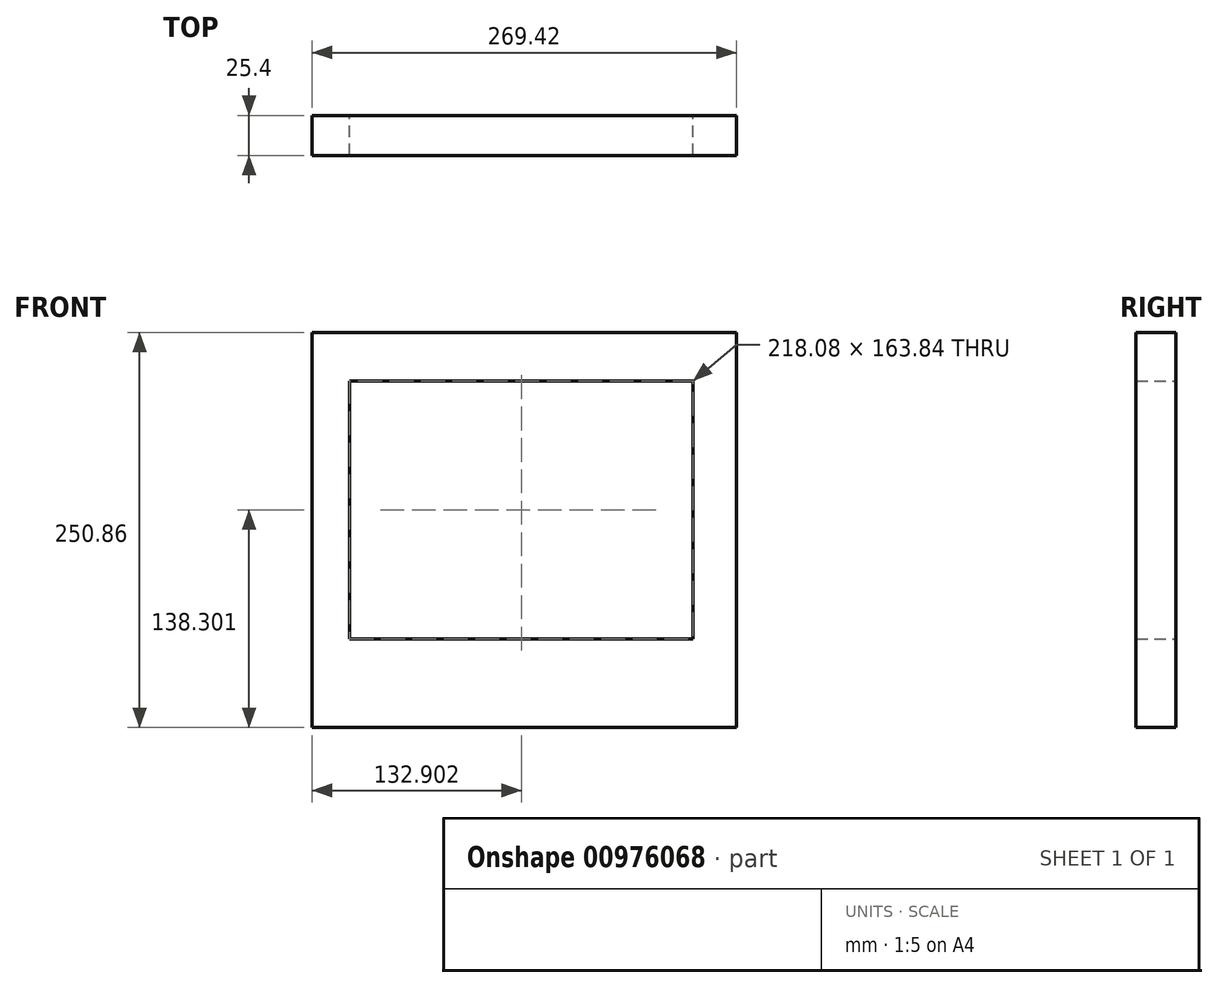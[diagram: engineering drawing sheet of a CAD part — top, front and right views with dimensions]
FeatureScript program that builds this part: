
annotation { "Feature Type Name" : "Feature", "Feature Type Description" : "" }
export const myFeature = defineFeature(function(context is Context, id is Id, definition is map)
    precondition{}
    {
        {
            var Q0;
            Q0=qCreatedBy(makeId("Front.planeOp"),FACE);
            var sketch = newSketch(context, id + "F0", { "sketchPlane" : qUnion([Q0])});
            skLineSegment(sketch, "E0.bottom", {"start": v(134.7, 125.43) * mm, "end": v(-134.7, 125.43) * mm});
            skLineSegment(sketch, "E0.top", {"start": v(134.7, -125.43) * mm, "end": v(-134.7, -125.43) * mm});
            skLineSegment(sketch, "E0.left", {"start": v(134.7, 125.43) * mm, "end": v(134.7, -125.43) * mm});
            skLineSegment(sketch, "E0.right", {"start": v(-134.7, 125.43) * mm, "end": v(-134.7, -125.43) * mm});
            skPoint(sketch, "E0.middle", {"position": v(0, 0) * mm});
            skLineSegment(sketch, "E1.bottom", {"start": v(-110.85, 94.8) * mm, "end": v(107.23, 94.8) * mm});
            skLineSegment(sketch, "E1.top", {"start": v(-110.85, -69.05) * mm, "end": v(107.23, -69.05) * mm});
            skLineSegment(sketch, "E1.left", {"start": v(-110.85, 94.8) * mm, "end": v(-110.85, -69.05) * mm});
            skLineSegment(sketch, "E1.right", {"start": v(107.23, 94.8) * mm, "end": v(107.23, -69.05) * mm});
            skSolve(sketch);
        }
        {
            var Q0;
            Q0=makeQuery(id+"F0.imprint","IMPRINT",FACE,{"disambiguationData":[TD([[makeQuery(id+"F0.imprint","IMPRINT",EDGE,{"derivedFrom":sQuery(id+"F0.wireOp",EDGE,"E0.bottom")}),1.0]])]});
            extrude(context, id + "F1", {"entities" : qUnion([Q0]), "depth" : 25.4 * mm, "offsetDistance" : 25.4 * mm});
        }
    });
